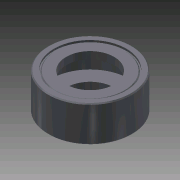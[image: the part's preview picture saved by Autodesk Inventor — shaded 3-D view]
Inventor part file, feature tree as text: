
AUTODESK INVENTOR PART (.ipt)
format: ipt  version: 2011 (Build 150239000, 239)  size: 144,896 bytes
history: native  units: in
note: dims shown in document units (in); Inventor stores cm internally (conversion verified against a paired STEP export)
features: sketch x6, extrude x5, chamfer x4, plane x3, revolve x1
ambient origin geometry x8: Origin, YZ Plane, XZ Plane, XY Plane, X Axis, Y Axis, Z Axis, Center Point
bodies: Solid1 (feature_tree)
feature tree (19):
  revolve  "Revolution1"  [1 undecoded]
  plane  "Work Plane1"
  extrude  "Extrusion1"  TaperAngle=90.0deg  [1 undecoded]
  plane  "Work Plane2"
  extrude  "Extrusion2"  Depth=0.5in
  plane  "Work Plane3"
  extrude  "Extrusion3"  [1 undecoded]
  extrude  "Extrusion4"  Depth=0.0756in TaperAngle=0.0deg
  chamfer  "Chamfer1"  Distance=0.815in
  extrude  "Extrusion5"  Depth=0.2018in TaperAngle=0.0deg
  chamfer  "Chamfer2"  Distance=0.01in
  chamfer  "Chamfer3"  Distance=0.01in
  chamfer  "Chamfer4"  Distance=0.01in Angle=45.0deg
  sketch  "Sketch1"  dims[d0=0.373in d1=0.06in]
  sketch  "Sketch2"  dims[d2=0.4375in d3=90.0deg]
  sketch  "Sketch3"  dims[d4=-0.01in d5=0.5in]
  sketch  "Sketch4"  dims[d6=0.0756in d7=0.0in d8=-0.01in]
  sketch  "Sketch5"  dims[d9=0.5in d10=0.0756in d11=0.0in]
  sketch  "Sketch6"  dims[d12=0.0in d13=0.815in d14=0.2018in d15=0.0in d16=0.01in d17=0.01in d18=0.0in d19=0.01in d20=0.125in d21=45.0deg d22=0.01in d23=0.01in d24=0.0in d25=0.01in d26=0.125in d27=45.0deg d28=0.01in d29=0.125in d30=45.0deg d31=0.01in d32=0.125in d33=45.0deg d34=0.875in d35=0.875in]
note: 3 required parameter values undecoded (feature->parameter linkage not recoverable at this tier; creation-order binding heuristic only, values carry confidence <= 0.55)